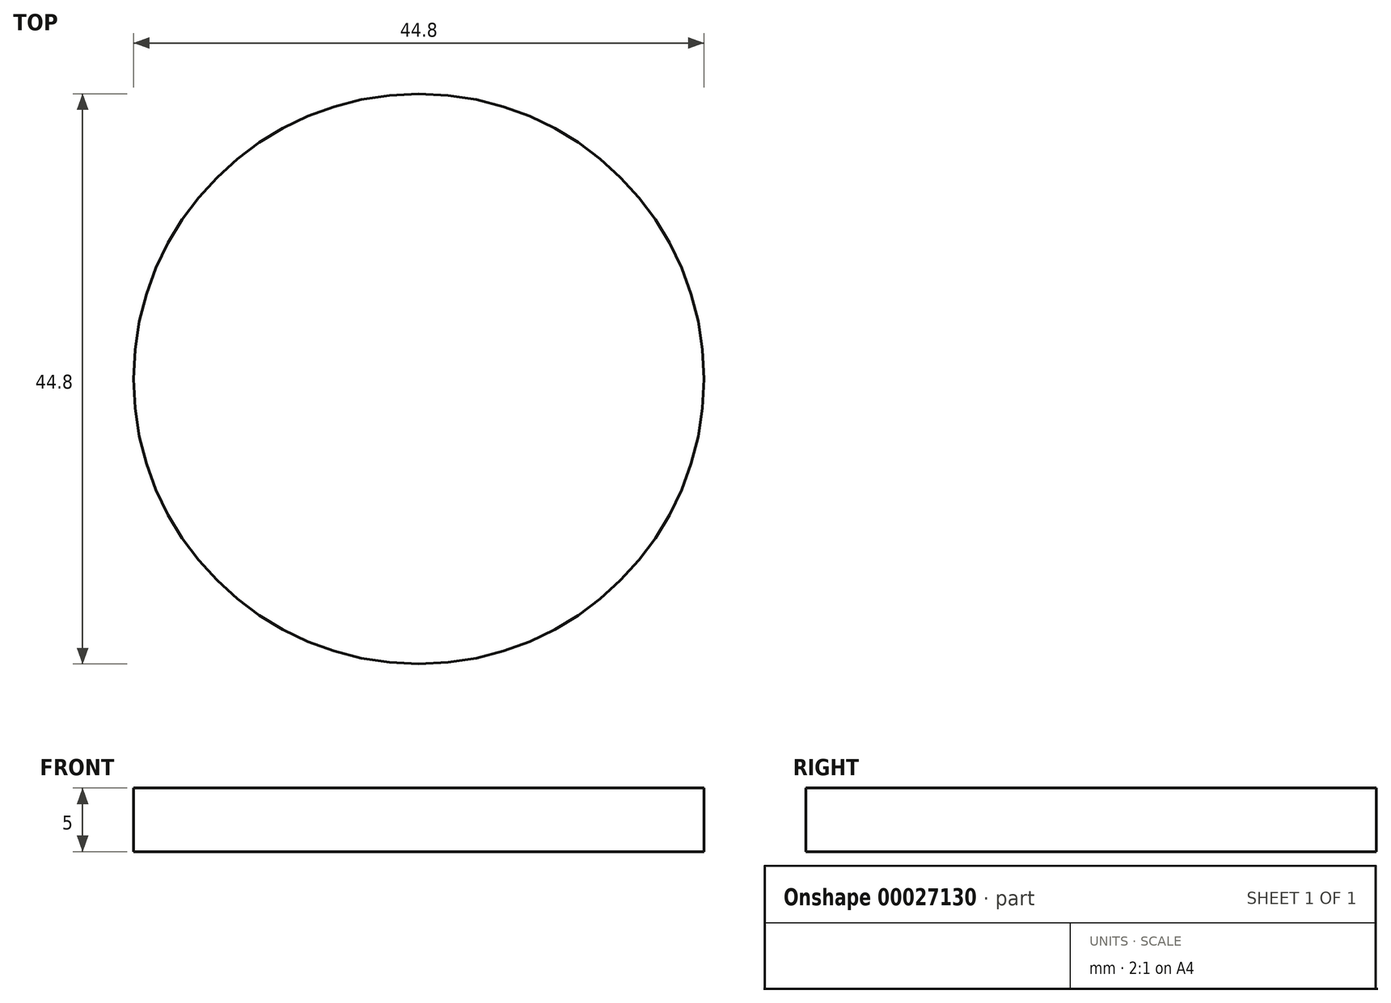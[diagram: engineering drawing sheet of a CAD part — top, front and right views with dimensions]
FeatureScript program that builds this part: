
annotation { "Feature Type Name" : "Feature", "Feature Type Description" : "" }
export const myFeature = defineFeature(function(context is Context, id is Id, definition is map)
    precondition{}
    {
        {
            var Q0;
            Q0=qCreatedBy(makeId("Top.planeOp"),FACE);
            var sketch = newSketch(context, id + "F0", { "sketchPlane" : qUnion([Q0])});
            skCircle(sketch, "E0", {"center": v(0, 0) * mm, "radius": 22.4 * mm});
            skSolve(sketch);
        }
        {
            var Q0;
            Q0=makeQuery(id+"F0.imprint","IMPRINT",FACE,{"disambiguationData":[TD([[makeQuery(id+"F0.imprint","IMPRINT",EDGE,{"derivedFrom":sQuery(id+"F0.wireOp",EDGE,"E0")}),1.0]])]});
            extrude(context, id + "F1", {"entities" : qUnion([Q0]), "depth" : 5 * mm});
        }
    });
